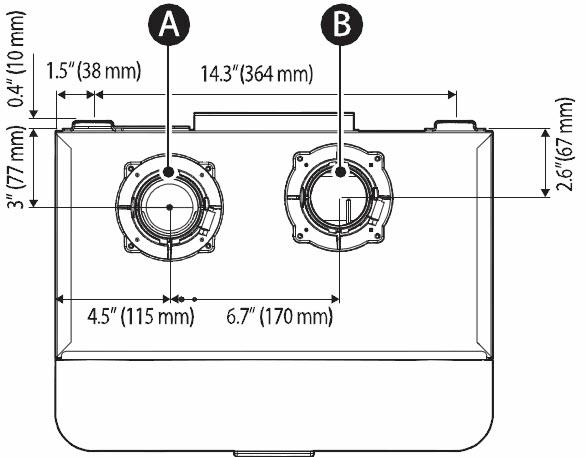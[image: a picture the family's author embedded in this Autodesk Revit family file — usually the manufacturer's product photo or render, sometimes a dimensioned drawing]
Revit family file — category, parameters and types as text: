
# Revit family: Water_Heater-Racks-Navien-NPE-10_Unit_Back_to_Back---
name_source: partatom
category: Mechanical Equipment
revit_build: Autodesk Revit 2016 (Build: 20150220_1215(x64)
units: mm (PartAtom-declared; Revit-internal decimal feet)

## family parameters
Cut with Voids When Loaded = No
Host = Face
OmniClass Number = 23.65.35.11
OmniClass Title = Supply Water Heaters
Part Type = Normal
Room Calculation Point = No
Round Connector Dimension = Use Diameter
Shared = No

## types (4) — shared parameters
2" Exhaust/Intake = Yes
3" Exhaust/Intake = No
Apparent Load = 0 VA
Assembly Code = D3010500
Certifications = Energy Star | AHRI | CSA | CSA | NFS
Cold Water Inlet = 1"
Configuration = NPE_B10_4B4B_2B
Default Elevation = 48 "
Depth = 23.8 "
Description = 10 Unit Back to Back
Exhaust = 2"
Finish = Metal - Navien - White
Flow Rate = 1 GPM
Flow Rate Note = 35°F (19°C) temp rise: 11.2 GPM (42 L/m) | 45°F (25°C) temp rise: 8.7 GPM (33 L/m) | 67°F (36°C) temp rise: NPE-240A: 5.6 GPM(21 L/m), NPE-240S: 5.7 GPM(22 L/m)
Frequency = 60 Hz
Gas Inlet = 1"
Heating Capacity = 120000.0 Btu/h
Heating Capacity Note = 19,900–199,900 (BTU/H)
Height = 65.5 "
Hot Water Outlet = 1"
Ignition = Electronic ignition
Installation Type = Indoor
Intake = 2"
Keynote = 22 33 00.A1
Manifold(s) = (1) 30019039A + (2) 30019042A
Manufacturer = Navien, Inc.
Manufacturer Fax Number = (949) 420-0430
Natural Gas Manifold Pressure = -0.05" WC to -0.58" WC
Natural Gas Supply Pressure = 3.5"–10.5" WC
Number of Poles = 1
Phase = 1
Power Factor = 1
Product Documentation Link = https://www.navieninc.com
Product Name = NPE Series Tankless Water Heaters w/ Racks
Product Page URL = https://www.navieninc.com
Propane Gas Manifold Pressure = -0.10" WC to -0.78" WC
Propane Gas Supply Pressure = 8"–13" WC
Rack(s) = (2) GFFM-KDIZUS-003 + (3) GFFM-KDIZUS-004
Required Cascade Operation Accessory = (10) 30014367A (Common Vent Damper & Cascade Communication Cable) or (9) GXXX000546 (Individual Vent Cascade Communication Cable)
URL = https://www.navieninc.com
Venting = Exhaust: 2" PVC, CPVC, PP, SS / 2" special gas vent type BH (Class II, A/B/C) | Intake: 2" PVC, CPVC, PP, SS / 2" special gas vent type BH (Class II, A/B/C) | Vent clearances: 0" to combustibles
Venting Type = Forced draft direct vent
Version = 2016 - v1.0.a
Voltage = 120 V
Water Pressure = 15–150 PSI
Wi-Fi Ready = NaviLink Wi-Fi Control: PBCM-AS-001
Width = 122.3 "

## per-type parameters (varying)
| type | Constraints | Model | Natural Gas | Propane Gas | Recirculation Inlet | Recirculation Inlet Visibility | Tankless Water Heaters | Weight |
| Natural Gas - Recirculating System - NPE-240A(Advanced)-NG | 6 | (10) NPE-240A-NG | Yes | No | 0" | Yes | (10) NPE-240A-NG | 82.00 lbf |
| Natural Gas - NPE-240S(Standard)-NG | 7 | (10) NPE-240S-NG | Yes | No | 1" | No | (10) NPE-240S-NG | 75.00 lbf |
| Propane Gas - Recirculating System - NPE-240A(Advanced)-LPG | 6 | (10) NPE-240A-LPG | No | Yes | 0" | Yes | (10) NPE-240A-LPG | 82.00 lbf |
| Propane Gas - NPE-240S(Standard)-LPG | 7 | (10) NPE-240S-LPG | No | Yes | 1" | No | (10) NPE-240S-LPG | 75.00 lbf |

## geometry (parser evidence)
native form markers: Sweep x21
no freeform markers — native parametric forms only
